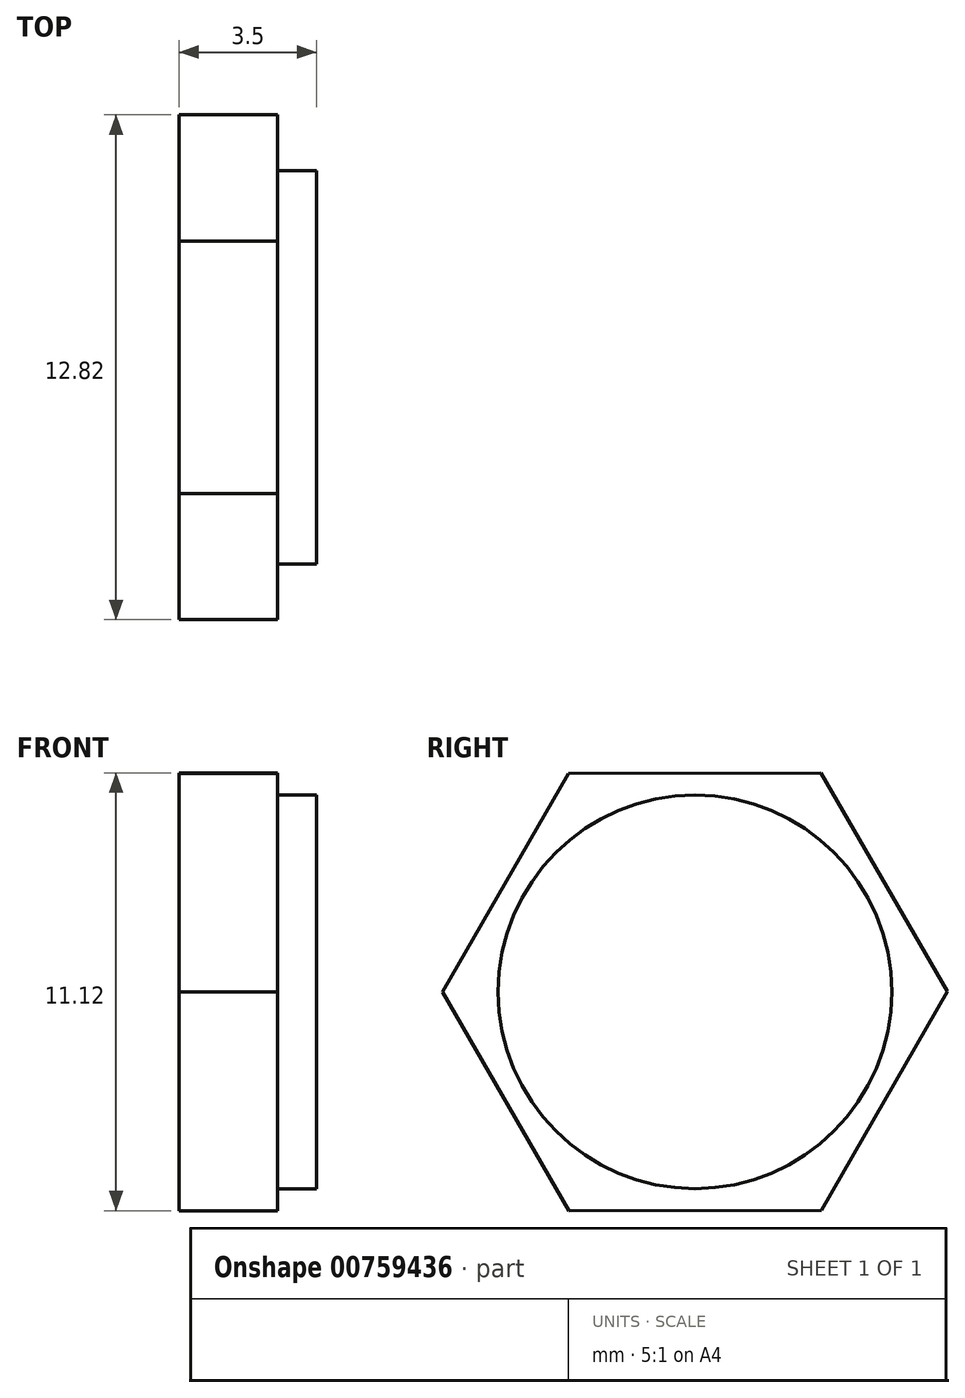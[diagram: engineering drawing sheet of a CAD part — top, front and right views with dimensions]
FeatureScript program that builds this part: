
annotation { "Feature Type Name" : "Feature", "Feature Type Description" : "" }
export const myFeature = defineFeature(function(context is Context, id is Id, definition is map)
    precondition{}
    {
        {
            var Q0;
            Q0=qCreatedBy(makeId("Right.planeOp"),FACE);
            var sketch = newSketch(context, id + "F0", { "sketchPlane" : qUnion([Q0])});
            skCircle(sketch, "E0.cCircle", {"center": v(0, 0) * mm, "radius": 5.55 * mm, "construction": true});
            skLineSegment(sketch, "E0.0", {"start": v(-3.2, -5.56) * mm, "end": v(-6.41, 0) * mm});
            skLineSegment(sketch, "E0.1", {"start": v(-6.41, 0) * mm, "end": v(-3.21, 5.55) * mm});
            skLineSegment(sketch, "E0.2", {"start": v(-3.21, 5.55) * mm, "end": v(3.2, 5.56) * mm});
            skLineSegment(sketch, "E0.3", {"start": v(3.2, 5.56) * mm, "end": v(6.41, 0) * mm});
            skLineSegment(sketch, "E0.4", {"start": v(6.41, 0) * mm, "end": v(3.21, -5.55) * mm});
            skLineSegment(sketch, "E0.5", {"start": v(3.21, -5.55) * mm, "end": v(-3.2, -5.56) * mm});
            skPoint(sketch, "E0.0.midPoint", {"position": v(-4.8, -2.78) * mm});
            skSolve(sketch);
        }
        {
            var Q0;
            Q0 = qSketchRegion(id + "F0", true);
            extrude(context, id + "F1", {"entities" : qUnion([Q0]), "endBound" : BoundingType.SYMMETRIC, "depth" : 2.5 * mm, "offsetDistance" : 25 * mm});
        }
        {
            var Q0;
            Q0=makeQuery(id+"F1.opExtrude","CAP_FACE",FACE,{"disambiguationData":[OSD([sQuery(id+"F0.wireOp",EDGE,"E0.0"),sQuery(id+"F0.wireOp",EDGE,"E0.1"),sQuery(id+"F0.wireOp",EDGE,"E0.2"),sQuery(id+"F0.wireOp",EDGE,"E0.3"),sQuery(id+"F0.wireOp",EDGE,"E0.4"),sQuery(id+"F0.wireOp",EDGE,"E0.5")])],"isStart":false});
            var sketch = newSketch(context, id + "F2", { "sketchPlane" : qUnion([Q0])});
            skCircle(sketch, "E1", {"center": v(0, 0) * mm, "radius": 5 * mm});
            skSolve(sketch);
        }
        {
            var Q0;
            Q0 = qSketchRegion(id + "F2", true);
            extrude(context, id + "F3", {"entities" : qUnion([Q0]), "operationType" : NewBodyOperationType.ADD, "depth" : 1 * mm, "offsetDistance" : 25 * mm});
        }
    });
